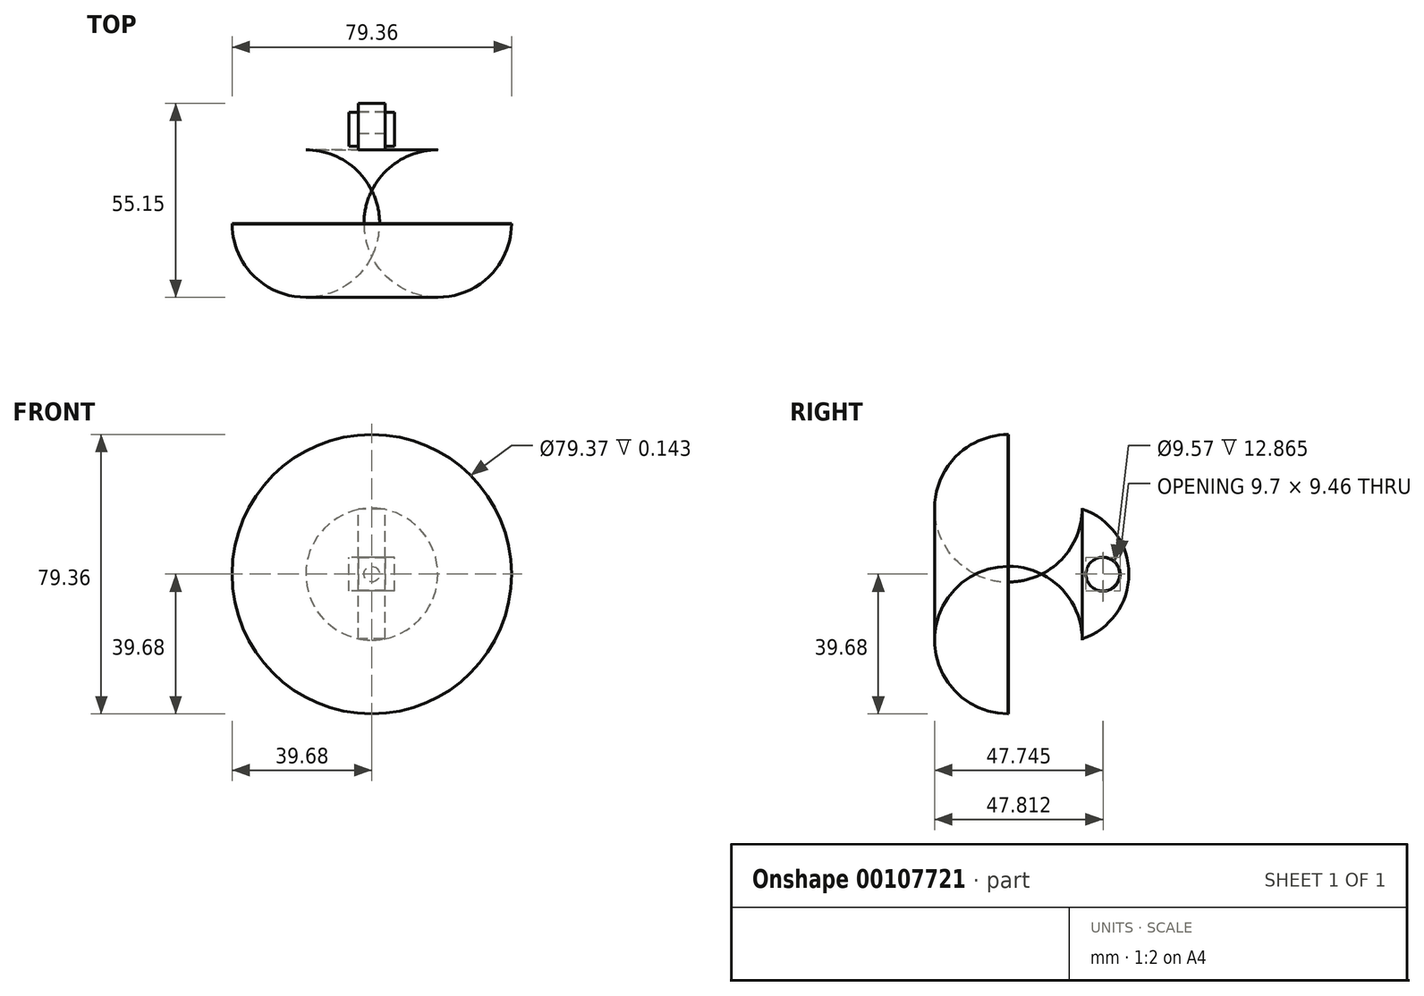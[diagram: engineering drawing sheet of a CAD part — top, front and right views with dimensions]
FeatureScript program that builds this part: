
annotation { "Feature Type Name" : "Feature", "Feature Type Description" : "" }
export const myFeature = defineFeature(function(context is Context, id is Id, definition is map)
    precondition{}
    {
        {
            var Q0;
            Q0=qCreatedBy(makeId("Front.planeOp"),FACE);
            var sketch = newSketch(context, id + "F0", { "sketchPlane" : qUnion([Q0])});
            skCircle(sketch, "E0", {"center": v(0, 0) * mm, "radius": 39.68 * mm});
            skSolve(sketch);
        }
        {
            var Q0;
            Q0=makeQuery(id+"F0.imprint","IMPRINT",FACE,{"disambiguationData":[TD([[makeQuery(id+"F0.imprint","IMPRINT",EDGE,{"derivedFrom":sQuery(id+"F0.wireOp",EDGE,"E0")}),1.0]])]});
            extrude(context, id + "F1", {"entities" : qUnion([Q0]), "oppositeDirection" : true, "depth" : 21.1 * mm});
        }
        {
            var Q0;
            Q0=makeQuery(id+"F1.opExtrude","CAP_EDGE",EDGE,{"disambiguationData":[OSD([sQuery(id+"F0.wireOp",EDGE,"E0")])],"isStart":false});
            fillet(context, id + "F2", {"entities" : qUnion([Q0]), "radius" : 20.96 * mm, "tangentPropagation" : true, "allowEdgeOverflow" : false});
        }
        {
            var Q0;
            Q0=qCreatedBy(makeId("Right.planeOp"),FACE);
            var sketch = newSketch(context, id + "F3", { "sketchPlane" : qUnion([Q0])});
            skCircle(sketch, "E1", {"center": v(27.04, 0) * mm, "radius": 4.81 * mm});
            skCircle(sketch, "E2", {"center": v(14.87, 0.05) * mm, "radius": 19.47 * mm});
            skLineSegment(sketch, "E3", {"start": v(14.87, 0.05) * mm, "end": v(14.87, 19.52) * mm});
            skLineSegment(sketch, "E4", {"start": v(14.87, 19.52) * mm, "end": v(14.87, -19.42) * mm});
            skSolve(sketch);
        }
        {
            var Q0;
            Q0=makeQuery(id+"F3.imprint","IMPRINT",FACE,{"disambiguationData":[TD([[makeQuery(id+"F3.imprint","IMPRINT",EDGE,{"derivedFrom":sQuery(id+"F3.wireOp",EDGE,"E1")}),-1.0]])]});
            extrude(context, id + "F4", {"entities" : qUnion([Q0]), "operationType" : NewBodyOperationType.ADD, "endBound" : BoundingType.SYMMETRIC, "depth" : 7.62 * mm});
        }
        {
            var Q0;
            Q0=qCreatedBy(makeId("Right.planeOp"),FACE);
            var sketch = newSketch(context, id + "F5", { "sketchPlane" : qUnion([Q0])});
            skCircle(sketch, "E5", {"center": v(26.94, 0) * mm, "radius": 4.78 * mm});
            skSolve(sketch);
        }
        {
            var Q0;
            Q0 = qSketchRegion(id + "F5", true);
            extrude(context, id + "F6", {"entities" : qUnion([Q0]), "operationType" : NewBodyOperationType.ADD, "endBound" : BoundingType.SYMMETRIC, "depth" : 12.86 * mm});
        }
    });
